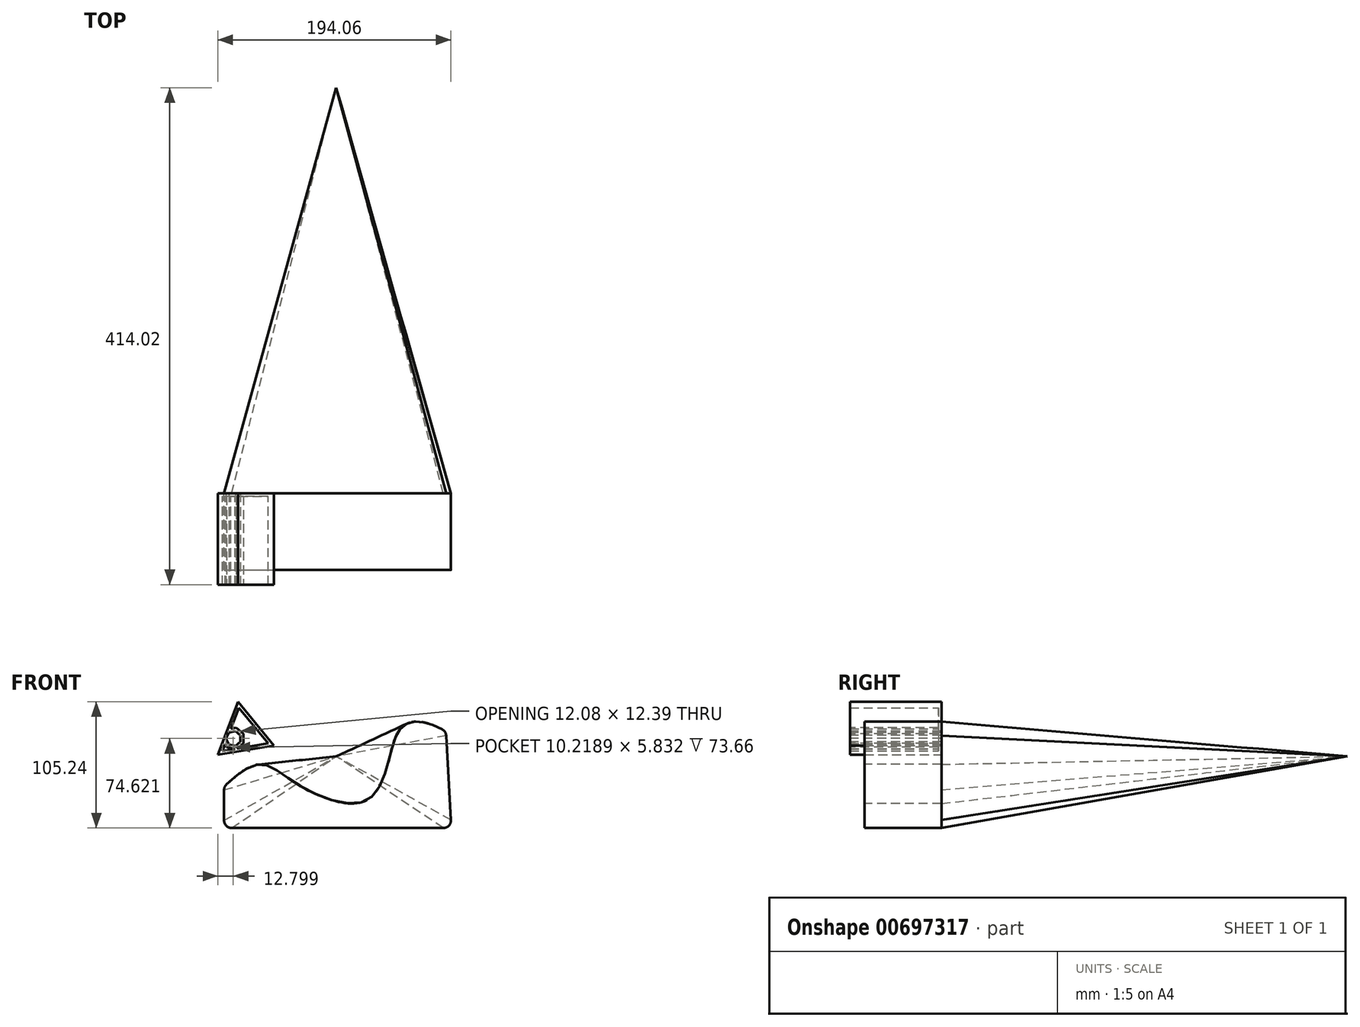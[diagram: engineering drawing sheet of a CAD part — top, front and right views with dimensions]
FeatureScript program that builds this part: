
annotation { "Feature Type Name" : "Feature", "Feature Type Description" : "" }
export const myFeature = defineFeature(function(context is Context, id is Id, definition is map)
    precondition{}
    {
        {
            var Q0;
            Q0=qCreatedBy(makeId("Front.planeOp"),FACE);
            var sketch = newSketch(context, id + "F0", { "sketchPlane" : qUnion([Q0])});
            skCircle(sketch, "E0.cCircle", {"center": v(-56.32, 18.58) * mm, "radius": 13.65 * mm, "construction": true});
            skLineSegment(sketch, "E0.0", {"start": v(-77.44, 1.3) * mm, "end": v(-60.73, 45.52) * mm});
            skLineSegment(sketch, "E0.1", {"start": v(-60.73, 45.52) * mm, "end": v(-30.78, 8.94) * mm});
            skLineSegment(sketch, "E0.2", {"start": v(-30.78, 8.94) * mm, "end": v(-77.44, 1.3) * mm});
            skPoint(sketch, "E0.0.midPoint", {"position": v(-69.09, 23.4) * mm});
            skSolve(sketch);
        }
        {
            var Q0;
            Q0=makeQuery(id+"F0.imprint","IMPRINT",FACE,{"disambiguationData":[TD([[makeQuery(id+"F0.imprint","IMPRINT",EDGE,{"derivedFrom":sQuery(id+"F0.wireOp",EDGE,"E0.0")}),-1.0]])]});
            extrude(context, id + "F1", {"entities" : qUnion([Q0]), "depth" : 76.2 * mm, "offsetDistance" : 25.4 * mm});
        }
        {
            var Q0;
            Q0=makeQuery(id+"F1.opExtrude","CAP_FACE",FACE,{"disambiguationData":[OSD([sQuery(id+"F0.wireOp",EDGE,"E0.0"),sQuery(id+"F0.wireOp",EDGE,"E0.1"),sQuery(id+"F0.wireOp",EDGE,"E0.2")])],"isStart":false});
            var sketch = newSketch(context, id + "F2", { "sketchPlane" : qUnion([Q0])});
            skCircle(sketch, "E1.cCircle", {"center": v(-64.33, 14.9) * mm, "radius": 5.73 * mm, "construction": true});
            skLineSegment(sketch, "E1.0", {"start": v(-58.6, 17.66) * mm, "end": v(-58.6, 12.14) * mm});
            skLineSegment(sketch, "E1.1", {"start": v(-58.6, 12.14) * mm, "end": v(-62.91, 8.7) * mm});
            skLineSegment(sketch, "E1.2", {"start": v(-62.91, 8.7) * mm, "end": v(-68.29, 9.93) * mm});
            skLineSegment(sketch, "E1.3", {"start": v(-68.29, 9.93) * mm, "end": v(-70.68, 14.9) * mm});
            skLineSegment(sketch, "E1.4", {"start": v(-70.68, 14.9) * mm, "end": v(-68.29, 19.87) * mm});
            skLineSegment(sketch, "E1.5", {"start": v(-68.29, 19.87) * mm, "end": v(-62.91, 21.1) * mm});
            skLineSegment(sketch, "E1.6", {"start": v(-62.91, 21.1) * mm, "end": v(-58.6, 17.66) * mm});
            skPoint(sketch, "E1.0.midPoint", {"position": v(-58.6, 14.9) * mm});
            skSolve(sketch);
        }
        {
            var Q0;
            Q0=makeQuery(id+"F2.imprint","IMPRINT",FACE,{"disambiguationData":[TD([[makeQuery(id+"F2.imprint","IMPRINT",EDGE,{"derivedFrom":sQuery(id+"F2.wireOp",EDGE,"E1.0")}),-1.0]])]});
            extrude(context, id + "F3", {"entities" : qUnion([Q0]), "operationType" : NewBodyOperationType.REMOVE, "oppositeDirection" : true, "depth" : 147.07 * mm, "offsetDistance" : 25.4 * mm});
        }
        {
            var Q0;
            Q0=makeQuery(id+"F1.opExtrude","CAP_FACE",FACE,{"disambiguationData":[OSD([sQuery(id+"F0.wireOp",EDGE,"E0.0"),sQuery(id+"F0.wireOp",EDGE,"E0.1"),sQuery(id+"F0.wireOp",EDGE,"E0.2")])],"isStart":false});
            shell(context, id + "F4", {"entities" : qUnion([Q0]), "thickness" : 2.54 * mm});
        }
        {
            var Q0;
            Q0=qCreatedBy(makeId("Front.planeOp"),FACE);
            var sketch = newSketch(context, id + "F5", { "sketchPlane" : qUnion([Q0])});
            skFitSpline(sketch, "E2", {"points": [v(-72.26, -25.1) * mm, v(-42.47, -6.67) * mm, v(-9.84, -23.97) * mm, v(45.2, -37.3) * mm, v(65.06, -2.7) * mm, v(75.28, 23.97) * mm, v(91.16, 28.8) * mm, v(112.44, 20.85) * mm], "startDerivative": vector(206.22, 186.1) * mm, "endDerivative": vector(160.1, -88.14) * mm});
            skLineSegment(sketch, "E3", {"start": v(-72.26, -27.94) * mm, "end": v(-72.26, -53.37) * mm});
            skLineSegment(sketch, "E4", {"start": v(-65.91, -59.72) * mm, "end": v(110.27, -59.72) * mm});
            skLineSegment(sketch, "E5", {"start": v(116.6, -53.02) * mm, "end": v(112.64, 17.29) * mm});
            skArc(sketch, "E6.filletArc", {"start": v(-70.15, -23.21) * mm, "mid": v(-71.7, -25.35) * mm, "end": v(-72.26, -27.94) * mm});
            skPoint(sketch, "E7.visualSharp", {"position": v(-72.26, -59.72) * mm});
            skArc(sketch, "E7.filletArc", {"start": v(-72.26, -53.37) * mm, "mid": v(-70.4, -57.86) * mm, "end": v(-65.91, -59.72) * mm});
            skPoint(sketch, "E8.visualSharp", {"position": v(116.98, -59.72) * mm});
            skArc(sketch, "E8.filletArc", {"start": v(110.27, -59.72) * mm, "mid": v(114.88, -57.74) * mm, "end": v(116.6, -53.02) * mm});
            skArc(sketch, "E9.filletArc", {"start": v(112.64, 17.29) * mm, "mid": v(111.63, 20.4) * mm, "end": v(109.2, 22.58) * mm});
            skSolve(sketch);
        }
        {
            var Q0;
            Q0=makeQuery(id+"F5.imprint","IMPRINT",FACE,{"disambiguationData":[TD([[makeQuery(id+"F5.imprint","IMPRINT",EDGE,{"derivedFrom":sQuery(id+"F5.wireOp",EDGE,"E2")}),-1.0]])]});
            extrude(context, id + "F6", {"entities" : qUnion([Q0]), "depth" : 64 * mm, "offsetDistance" : 25.4 * mm});
        }
        {
            var Q0;
            Q0=makeQuery(id+"F6.opExtrude","CAP_FACE",FACE,{"disambiguationData":[OSD([sQuery(id+"F5.wireOp",EDGE,"E2"),sQuery(id+"F5.wireOp",EDGE,"E3"),sQuery(id+"F5.wireOp",EDGE,"E4"),sQuery(id+"F5.wireOp",EDGE,"E5"),sQuery(id+"F5.wireOp",EDGE,"E6.filletArc"),sQuery(id+"F5.wireOp",EDGE,"E7.filletArc"),sQuery(id+"F5.wireOp",EDGE,"E8.filletArc"),sQuery(id+"F5.wireOp",EDGE,"E9.filletArc")])],"isStart":true});
            cPlane(context, id + "F7", {"entities" : qUnion([Q0]), "cplaneType" : CPlaneType.OFFSET, "offset" : 337.82 * mm, "width" : 152.4 * mm, "height" : 152.4 * mm});
        }
        {
            var Q0;
            Q0=qCreatedBy(id+"F7.planeOp",FACE);
            var sketch = newSketch(context, id + "F8", { "sketchPlane" : qUnion([Q0])});
            skPoint(sketch, "E10", {"position": v(-21.1, 0) * mm});
            skSolve(sketch);
        }
        {
            var Q1;
            Q1=makeQuery(id+"F6.opExtrude","CAP_FACE",FACE,{"disambiguationData":[OSD([sQuery(id+"F5.wireOp",EDGE,"E2"),sQuery(id+"F5.wireOp",EDGE,"E3"),sQuery(id+"F5.wireOp",EDGE,"E4"),sQuery(id+"F5.wireOp",EDGE,"E5"),sQuery(id+"F5.wireOp",EDGE,"E6.filletArc"),sQuery(id+"F5.wireOp",EDGE,"E7.filletArc"),sQuery(id+"F5.wireOp",EDGE,"E8.filletArc"),sQuery(id+"F5.wireOp",EDGE,"E9.filletArc")])],"isStart":true});
            var Q2;
            Q2=sQuery(id+"F8.wireOp",VERTEX,"E10");
            loft(context, id + "F9", {"operationType" : NewBodyOperationType.ADD, "sheetProfilesArray" : [{ "sheetProfileEntities" : qUnion([Q1]) }, { "sheetProfileEntities" : qUnion([Q2]) }]});
        }
    });
